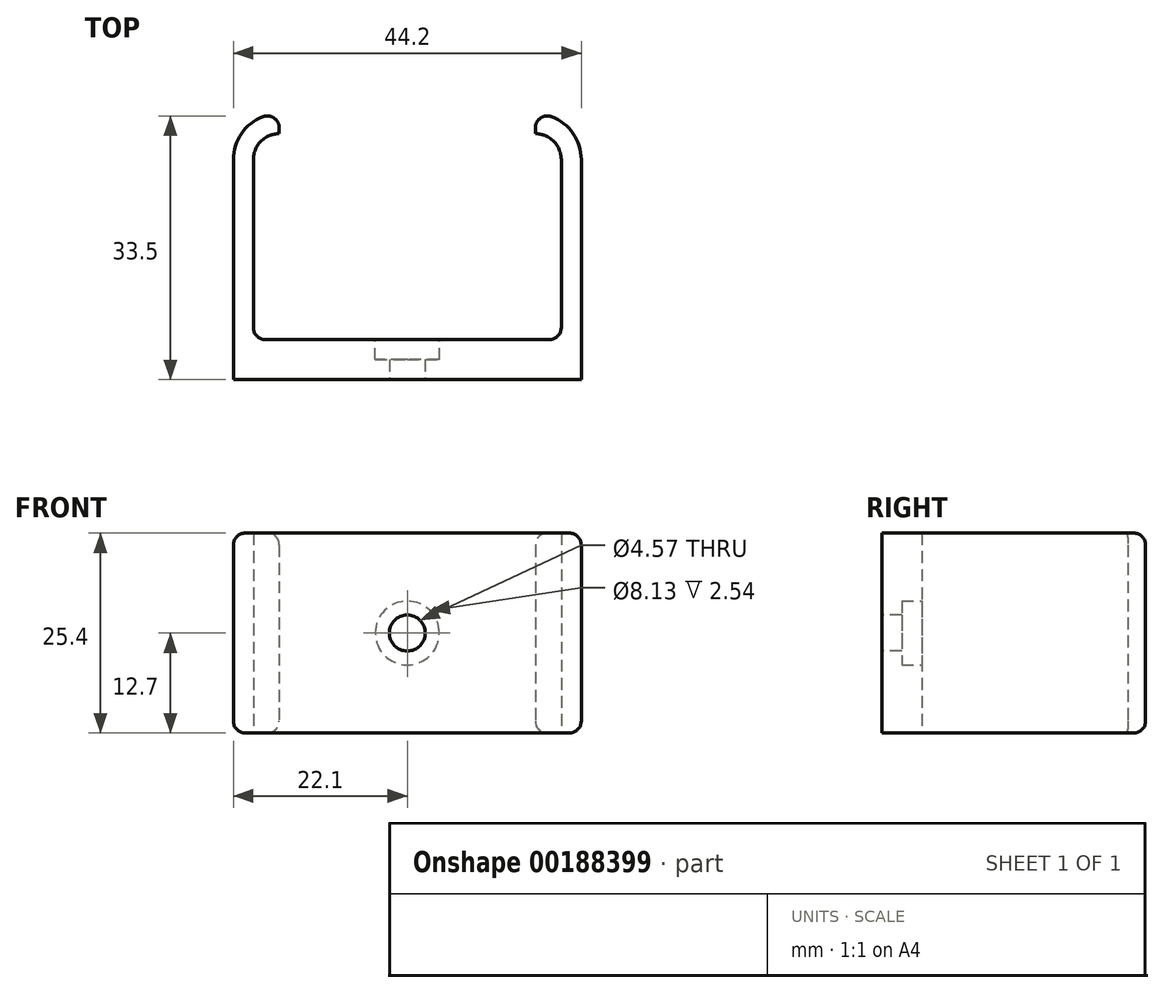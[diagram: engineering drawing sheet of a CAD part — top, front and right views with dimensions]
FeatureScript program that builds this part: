
annotation { "Feature Type Name" : "Feature", "Feature Type Description" : "" }
export const myFeature = defineFeature(function(context is Context, id is Id, definition is map)
    precondition{}
    {
        {
            var Q0;
            Q0=qCreatedBy(makeId("Top.planeOp"),FACE);
            var sketch = newSketch(context, id + "F0", { "sketchPlane" : qUnion([Q0])});
            skLineSegment(sketch, "E0", {"start": v(-22.1, 22.86) * mm, "end": v(-22.1, -5.08) * mm});
            skLineSegment(sketch, "E1", {"start": v(-22.1, -5.08) * mm, "end": v(22.1, -5.08) * mm});
            skLineSegment(sketch, "E2", {"start": v(22.1, -5.08) * mm, "end": v(22.1, 22.86) * mm});
            skArc(sketch, "E3", {"start": v(-16.26, 28.7) * mm, "mid": v(-20.39, 27) * mm, "end": v(-22.1, 22.86) * mm});
            skArc(sketch, "E4", {"start": v(-16.26, 26.16) * mm, "mid": v(-18.6, 25.2) * mm, "end": v(-19.56, 22.86) * mm});
            skLineSegment(sketch, "E5", {"start": v(-19.56, 22.86) * mm, "end": v(-19.56, 0) * mm});
            skLineSegment(sketch, "E6", {"start": v(-19.56, 0) * mm, "end": v(19.56, 0) * mm});
            skLineSegment(sketch, "E7", {"start": v(19.56, 0) * mm, "end": v(19.56, 22.86) * mm});
            skArc(sketch, "E8", {"start": v(19.56, 22.86) * mm, "mid": v(18.6, 25.2) * mm, "end": v(16.26, 26.16) * mm});
            skArc(sketch, "E9", {"start": v(22.1, 22.86) * mm, "mid": v(20.39, 27) * mm, "end": v(16.26, 28.7) * mm});
            skLineSegment(sketch, "E10", {"start": v(-16.26, 28.7) * mm, "end": v(-16.26, 26.16) * mm});
            skLineSegment(sketch, "E11", {"start": v(16.26, 28.7) * mm, "end": v(16.26, 26.16) * mm});
            skPoint(sketch, "E12", {"position": v(0, 0) * mm});
            skPoint(sketch, "E13", {"position": v(0, -5.08) * mm});
            skSolve(sketch);
        }
        {
            var Q0;
            Q0 = qSketchRegion(id + "F0", true);
            extrude(context, id + "F1", {"entities" : qUnion([Q0]), "offsetDistance" : 25.4 * mm, "depth" : 25.4 * mm});
        }
        {
            var Q0;
            Q0=makeQuery(id+"F1.opExtrude","SWEPT_FACE",FACE,{"disambiguationData":[OSD([sQuery(id+"F0.wireOp",EDGE,"E1")])]});
            var sketch = newSketch(context, id + "F2", { "sketchPlane" : qUnion([Q0])});
            skCircle(sketch, "E14", {"center": v(0, 12.7) * mm, "radius": 2.29 * mm});
            skLineSegment(sketch, "E15", {"start": v(0, 0) * mm, "end": v(0, 25.4) * mm, "construction": true});
            skSolve(sketch);
        }
        {
            var Q0;
            Q0 = qSketchRegion(id + "F2", true);
            var Q1;
            Q1=makeQuery(id+"F1.opExtrude","SWEPT_FACE",FACE,{"disambiguationData":[OSD([sQuery(id+"F0.wireOp",EDGE,"E6")])]});
            extrude(context, id + "F3", {"entities" : qUnion([Q0]), "operationType" : NewBodyOperationType.REMOVE, "endBound" : BoundingType.UP_TO_SURFACE, "oppositeDirection" : true, "endBoundEntityFace" : qUnion([Q1]), "depth" : 25.4 * mm});
        }
        {
            var Q0;
            Q0=makeQuery(id+"F1.opExtrude","SWEPT_FACE",FACE,{"disambiguationData":[OSD([sQuery(id+"F0.wireOp",EDGE,"E6")])]});
            var sketch = newSketch(context, id + "F4", { "sketchPlane" : qUnion([Q0])});
            skCircle(sketch, "E16", {"center": v(0, 12.7) * mm, "radius": 4.06 * mm});
            skSolve(sketch);
        }
        {
            var Q0;
            Q0 = qSketchRegion(id + "F4", true);
            extrude(context, id + "F5", {"entities" : qUnion([Q0]), "operationType" : NewBodyOperationType.REMOVE, "oppositeDirection" : true, "depth" : 2.54 * mm});
        }
        {
            var Q0;
            Q0=makeQuery(id+"F1.opExtrude","CAP_EDGE",EDGE,{"disambiguationData":[OSD([sQuery(id+"F0.wireOp",EDGE,"E3")])],"isStart":false});
            var Q1;
            Q1=makeQuery(id+"F1.opExtrude","CAP_EDGE",EDGE,{"disambiguationData":[OSD([sQuery(id+"F0.wireOp",EDGE,"E9")])],"isStart":false});
            var Q2;
            Q2=makeQuery(id+"F1.opExtrude","CAP_EDGE",EDGE,{"disambiguationData":[OSD([sQuery(id+"F0.wireOp",EDGE,"E9")])],"isStart":true});
            var Q3;
            Q3=makeQuery(id+"F1.opExtrude","CAP_EDGE",EDGE,{"disambiguationData":[OSD([sQuery(id+"F0.wireOp",EDGE,"E0")])],"isStart":true});
            var Q4;
            Q4=makeQuery(id+"F1.opExtrude","SWEPT_EDGE",EDGE,{"disambiguationData":[OSD([sQuery(id+"F0.wireOp",EDGE,"E5"),sQuery(id+"F0.wireOp",EDGE,"E6")])]});
            var Q5;
            Q5=makeQuery(id+"F1.opExtrude","SWEPT_EDGE",EDGE,{"disambiguationData":[OSD([sQuery(id+"F0.wireOp",EDGE,"E6"),sQuery(id+"F0.wireOp",EDGE,"E7")])]});
            var Q6;
            Q6=makeQuery(id+"F1.opExtrude","SWEPT_EDGE",EDGE,{"disambiguationData":[OSD([sQuery(id+"F0.wireOp",EDGE,"E3"),sQuery(id+"F0.wireOp",EDGE,"E10")])]});
            var Q7;
            Q7=makeQuery(id+"F1.opExtrude","SWEPT_EDGE",EDGE,{"disambiguationData":[OSD([sQuery(id+"F0.wireOp",EDGE,"E9"),sQuery(id+"F0.wireOp",EDGE,"E11")])]});
            var Q8;
            Q8=makeQuery(id+"F1.opExtrude","CAP_EDGE",EDGE,{"disambiguationData":[OSD([sQuery(id+"F0.wireOp",EDGE,"E10")])],"isStart":false});
            var Q9;
            Q9=makeQuery(id+"F1.opExtrude","CAP_EDGE",EDGE,{"disambiguationData":[OSD([sQuery(id+"F0.wireOp",EDGE,"E11")])],"isStart":false});
            var Q10;
            Q10=makeQuery(id+"F1.opExtrude","CAP_EDGE",EDGE,{"disambiguationData":[OSD([sQuery(id+"F0.wireOp",EDGE,"E11")])],"isStart":true});
            var Q11;
            Q11=makeQuery(id+"F1.opExtrude","CAP_EDGE",EDGE,{"disambiguationData":[OSD([sQuery(id+"F0.wireOp",EDGE,"E10")])],"isStart":true});
            fillet(context, id + "F6", {"entities" : qUnion([Q0, Q1, Q2, Q3, Q4, Q5, Q6, Q7, Q8, Q9, Q10, Q11]), "radius" : 1.52 * mm, "tangentPropagation" : true, "allowEdgeOverflow" : false});
        }
    });
